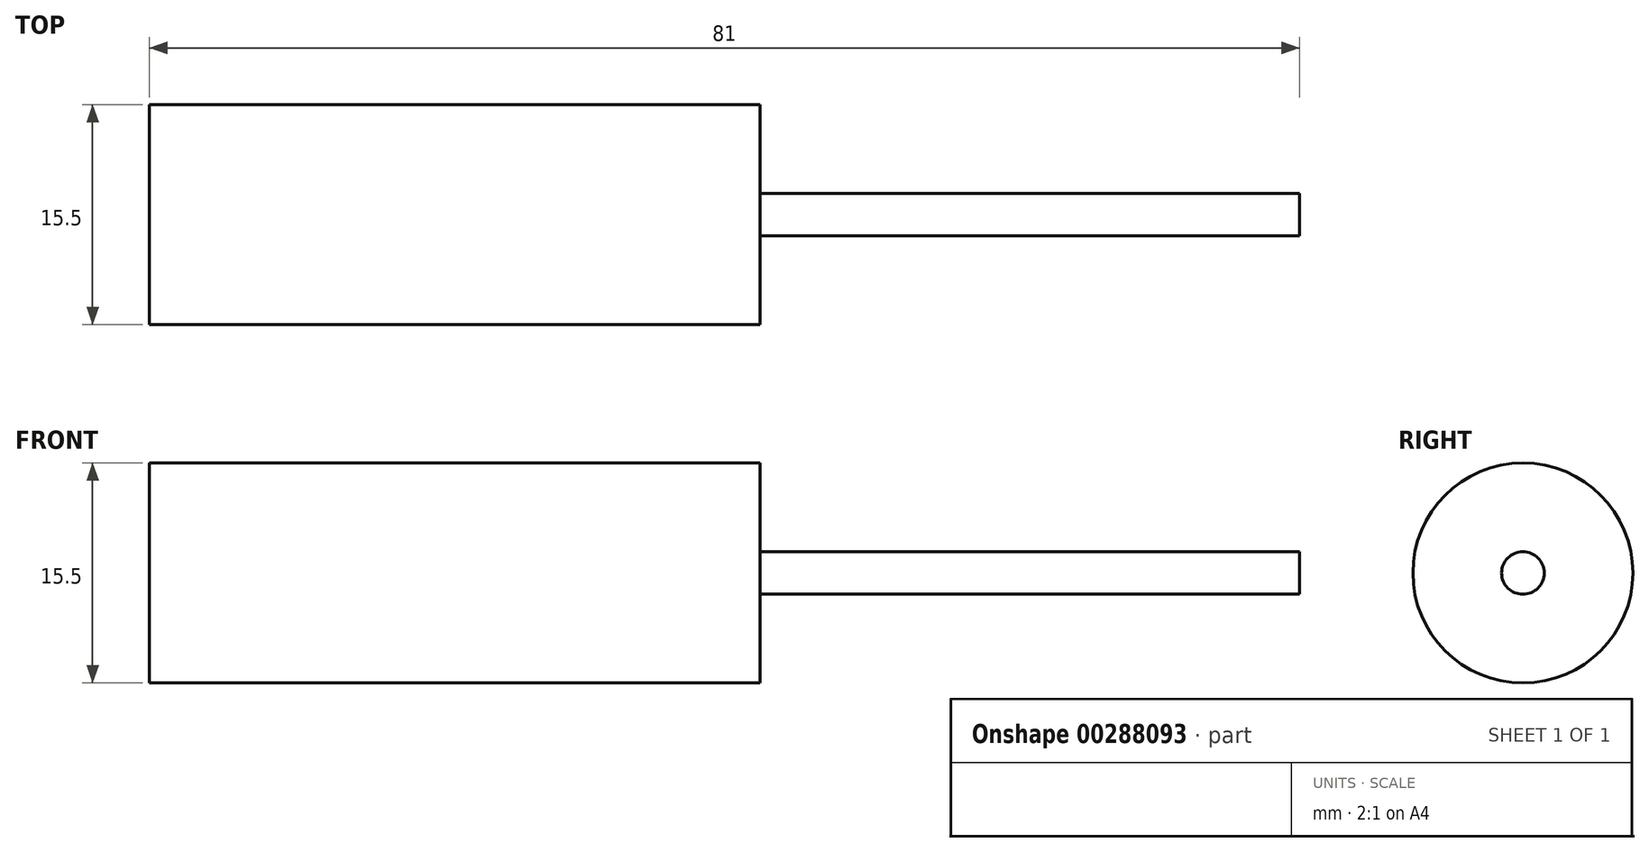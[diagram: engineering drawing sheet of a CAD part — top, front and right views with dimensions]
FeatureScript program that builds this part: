
annotation { "Feature Type Name" : "Feature", "Feature Type Description" : "" }
export const myFeature = defineFeature(function(context is Context, id is Id, definition is map)
    precondition{}
    {
        {
            var Q0;
            Q0=qCreatedBy(makeId("Right.planeOp"),FACE);
            var sketch = newSketch(context, id + "F0", { "sketchPlane" : qUnion([Q0])});
            skCircle(sketch, "E0", {"center": v(0, 0) * mm, "radius": 7.75 * mm});
            skCircle(sketch, "E1", {"center": v(0, 0) * mm, "radius": 1.5 * mm});
            skSolve(sketch);
        }
        {
            var Q0;
            Q0=qSketchRegion(id+"F0",true);
            extrude(context, id + "F1", {"entities" : qUnion([Q0]), "depth" : 43 * mm});
        }
        {
            var Q0;
            Q0=qCreatedBy(makeId("Right.planeOp"),FACE);
            var sketch = newSketch(context, id + "F2", { "sketchPlane" : qUnion([Q0])});
            skCircle(sketch, "E2", {"center": v(0, 0) * mm, "radius": 1.5 * mm});
            skSolve(sketch);
        }
        {
            var Q0;
            Q0=qSketchRegion(id+"F2",true);
            extrude(context, id + "F3", {"entities" : qUnion([Q0]), "operationType" : NewBodyOperationType.ADD, "depth" : 81 * mm});
        }
    });
